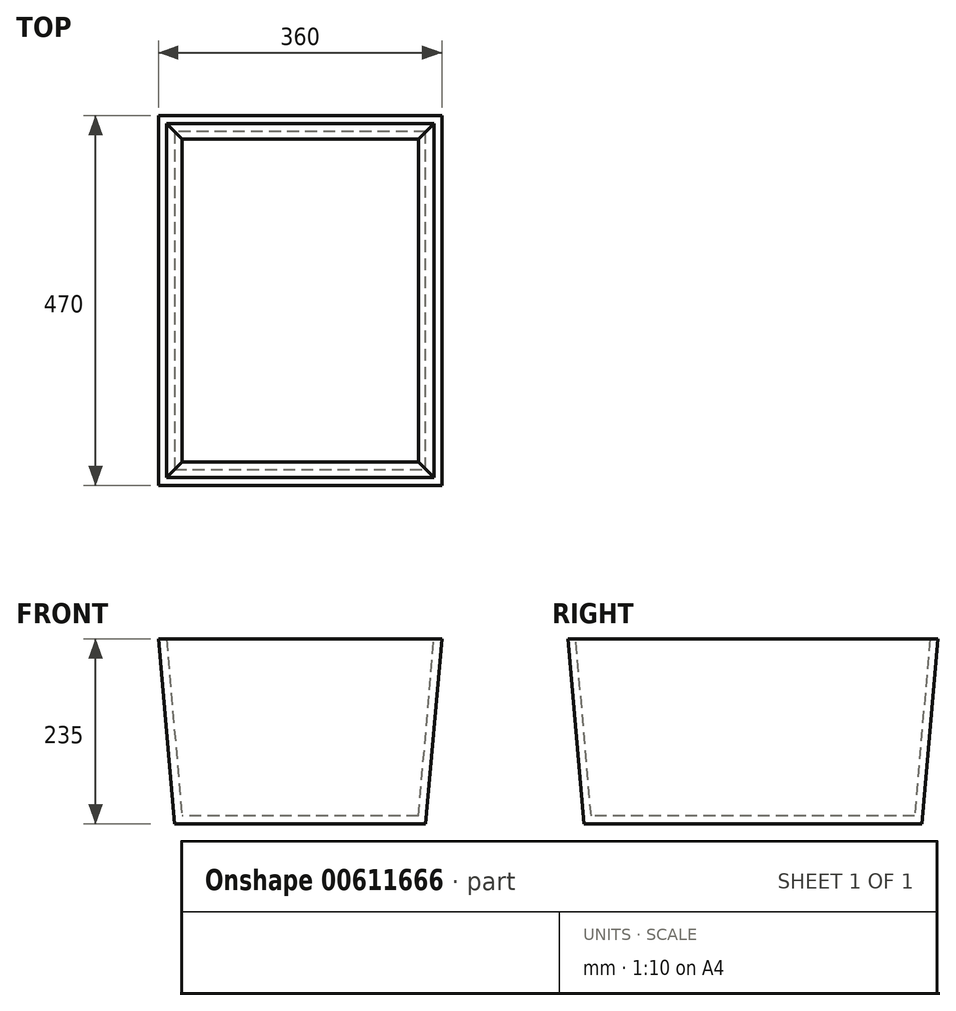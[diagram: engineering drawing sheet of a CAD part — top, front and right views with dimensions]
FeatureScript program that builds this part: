
annotation { "Feature Type Name" : "Feature", "Feature Type Description" : "" }
export const myFeature = defineFeature(function(context is Context, id is Id, definition is map)
    precondition{}
    {
        {
            var Q0;
            Q0=qCreatedBy(makeId("Top.planeOp"),FACE);
            var sketch = newSketch(context, id + "F0", { "sketchPlane" : qUnion([Q0])});
            skLineSegment(sketch, "E0.bottom", {"start": v(-180, 235) * mm, "end": v(180, 235) * mm});
            skLineSegment(sketch, "E0.top", {"start": v(-180, -235) * mm, "end": v(180, -235) * mm});
            skLineSegment(sketch, "E0.left", {"start": v(-180, 235) * mm, "end": v(-180, -235) * mm});
            skLineSegment(sketch, "E0.right", {"start": v(180, 235) * mm, "end": v(180, -235) * mm});
            skPoint(sketch, "E0.middle", {"position": v(0, 0) * mm});
            skSolve(sketch);
        }
        {
            var Q0;
            Q0 = qSketchRegion(id + "F0", true);
            extrude(context, id + "F1", {"entities" : qUnion([Q0]), "oppositeDirection" : true, "depth" : 235 * mm, "offsetDistance" : 25 * mm, "hasDraft" : true, "draftAngle" : 5 * degree, "draftPullDirection" : true});
        }
        {
            var Q0;
            Q0=makeQuery(id+"F1.opExtrude","CAP_FACE",FACE,{"disambiguationData":[OSD([sQuery(id+"F0.wireOp",EDGE,"E0.bottom"),sQuery(id+"F0.wireOp",EDGE,"E0.top"),sQuery(id+"F0.wireOp",EDGE,"E0.left"),sQuery(id+"F0.wireOp",EDGE,"E0.right")])],"isStart":true});
            shell(context, id + "F2", {"entities" : qUnion([Q0]), "thickness" : 10 * mm});
        }
    });
